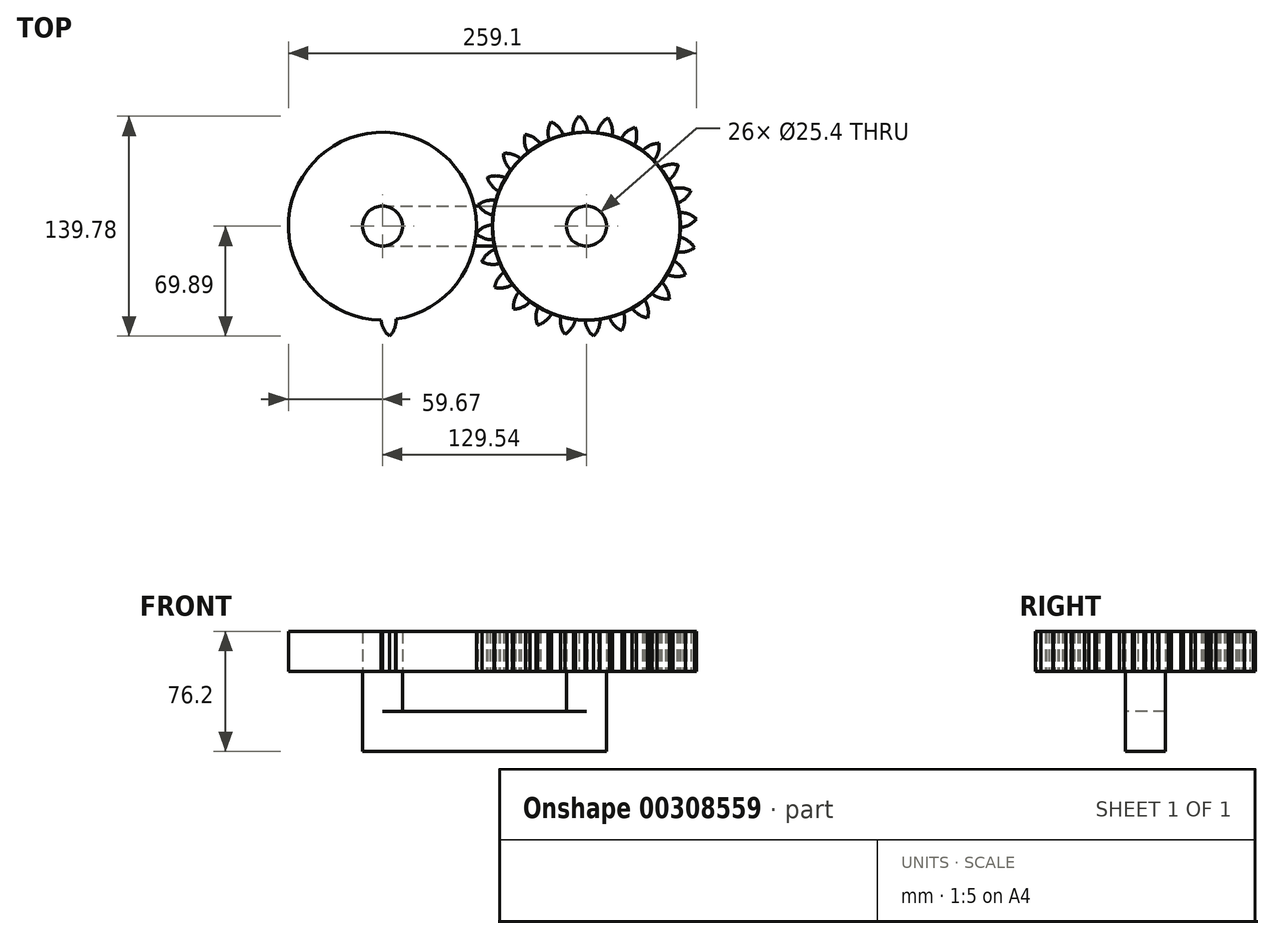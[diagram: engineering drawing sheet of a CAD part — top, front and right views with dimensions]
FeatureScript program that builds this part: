
annotation { "Feature Type Name" : "Feature", "Feature Type Description" : "" }
export const myFeature = defineFeature(function(context is Context, id is Id, definition is map)
    precondition{}
    {
        {
            var Q0;
            Q0=qCreatedBy(makeId("Top.planeOp"),FACE);
            var sketch = newSketch(context, id + "F0", { "sketchPlane" : qUnion([Q0])});
            skLineSegment(sketch, "E0.bottom", {"start": v(-22.49, 9.75) * mm, "end": v(107.05, 9.75) * mm});
            skLineSegment(sketch, "E0.top", {"start": v(-22.49, -15.65) * mm, "end": v(107.05, -15.65) * mm});
            skLineSegment(sketch, "E0.left", {"start": v(-22.49, 9.75) * mm, "end": v(-22.49, -15.65) * mm});
            skLineSegment(sketch, "E0.right", {"start": v(107.05, 9.75) * mm, "end": v(107.05, -15.65) * mm});
            skCircle(sketch, "E1", {"center": v(-22.49, -2.95) * mm, "radius": 12.7 * mm});
            skCircle(sketch, "E2", {"center": v(107.05, -2.95) * mm, "radius": 12.7 * mm});
            skSolve(sketch);
        }
        {
            var Q0;
            {var subQ0=sQuery(id+"F0.wireOp",EDGE,"E0.left");Q0=makeQuery(id+"F0.imprint","IMPRINT",FACE,{"disambiguationData":[TD([[makeQuery(id+"F0.imprint","IMPRINT",EDGE,{"derivedFrom":subQ0}),-1.0]])]});}
            var Q1;
            {var subQ0=sQuery(id+"F0.wireOp",EDGE,"E0.left");Q1=makeQuery(id+"F0.imprint","IMPRINT",FACE,{"disambiguationData":[TD([[makeQuery(id+"F0.imprint","IMPRINT",EDGE,{"derivedFrom":subQ0}),1.0]])]});}
            var Q2;
            {var subQ0=sQuery(id+"F0.wireOp",EDGE,"E0.bottom");Q2=makeQuery(id+"F0.imprint","IMPRINT",FACE,{"disambiguationData":[TD([[makeQuery(id+"F0.imprint","IMPRINT",EDGE,{"derivedFrom":subQ0}),-1.0]])]});}
            var Q3;
            {var subQ0=sQuery(id+"F0.wireOp",EDGE,"E0.right");Q3=makeQuery(id+"F0.imprint","IMPRINT",FACE,{"disambiguationData":[TD([[makeQuery(id+"F0.imprint","IMPRINT",EDGE,{"derivedFrom":subQ0}),-1.0]])]});}
            var Q4;
            {var subQ0=sQuery(id+"F0.wireOp",EDGE,"E0.right");Q4=makeQuery(id+"F0.imprint","IMPRINT",FACE,{"disambiguationData":[TD([[makeQuery(id+"F0.imprint","IMPRINT",EDGE,{"derivedFrom":subQ0}),1.0]])]});}
            extrude(context, id + "F1", {"entities" : qUnion([Q0, Q1, Q2, Q3, Q4]), "depth" : 25.4 * mm});
        }
        {
            var Q0;
            {var subQ0=sQuery(id+"F0.wireOp",EDGE,"E0.right");Q0=makeQuery(id+"F0.imprint","IMPRINT",FACE,{"disambiguationData":[TD([[makeQuery(id+"F0.imprint","IMPRINT",EDGE,{"derivedFrom":subQ0}),1.0]])]});}
            var Q1;
            {var subQ0=sQuery(id+"F0.wireOp",EDGE,"E0.right");Q1=makeQuery(id+"F0.imprint","IMPRINT",FACE,{"disambiguationData":[TD([[makeQuery(id+"F0.imprint","IMPRINT",EDGE,{"derivedFrom":subQ0}),-1.0]])]});}
            var Q2;
            {var subQ0=sQuery(id+"F0.wireOp",EDGE,"E0.left");Q2=makeQuery(id+"F0.imprint","IMPRINT",FACE,{"disambiguationData":[TD([[makeQuery(id+"F0.imprint","IMPRINT",EDGE,{"derivedFrom":subQ0}),1.0]])]});}
            var Q3;
            {var subQ0=sQuery(id+"F0.wireOp",EDGE,"E0.left");Q3=makeQuery(id+"F0.imprint","IMPRINT",FACE,{"disambiguationData":[TD([[makeQuery(id+"F0.imprint","IMPRINT",EDGE,{"derivedFrom":subQ0}),-1.0]])]});}
            extrude(context, id + "F2", {"entities" : qUnion([Q0, Q1, Q2, Q3]), "operationType" : NewBodyOperationType.ADD, "depth" : 50.8 * mm});
        }
        {
            var Q0;
            Q0=makeQuery(id+"F2.opExtrude","CAP_FACE",FACE,{"disambiguationData":[OSD([sQuery(id+"F0.wireOp",EDGE,"E2")])],"isStart":false});
            var sketch = newSketch(context, id + "F3", { "sketchPlane" : qUnion([Q0])});
            skCircle(sketch, "E3", {"center": v(107.05, -2.95) * mm, "radius": 12.7 * mm});
            skCircle(sketch, "E4", {"center": v(107.05, -2.95) * mm, "radius": 53.72 * mm, "construction": true});
            skCircle(sketch, "E5", {"center": v(107.05, -2.95) * mm, "radius": 58.67 * mm, "construction": true});
            skCircle(sketch, "E6", {"center": v(107.05, -2.95) * mm, "radius": 63.5 * mm, "construction": true});
            skLineSegment(sketch, "E7", {"start": v(107.05, -2.95) * mm, "end": v(107.05, -93.43) * mm, "construction": true});
            skLineSegment(sketch, "E8", {"start": v(107.05, -2.95) * mm, "end": v(112.98, -93.47) * mm, "construction": true});
            skCircle(sketch, "E9", {"center": v(107.05, -66.45) * mm, "radius": 14.6 * mm, "construction": true});
            skLineSegment(sketch, "E10", {"start": v(107.05, -66.45) * mm, "end": v(166.51, -66.45) * mm, "construction": true});
            skLineSegment(sketch, "E11", {"start": v(173.53, -42.25) * mm, "end": v(107.05, -66.45) * mm, "construction": true});
            skCircle(sketch, "E12", {"center": v(120.77, -61.45) * mm, "radius": 14.6 * mm, "construction": true});
            skCircle(sketch, "E13", {"center": v(107.05, -2.95) * mm, "radius": 59.67 * mm});
            skArc(sketch, "E14", {"start": v(107.05, -66.45) * mm, "mid": v(108.9, -69.97) * mm, "end": v(111.63, -72.84) * mm});
            skArc(sketch, "E15", {"start": v(106.22, -62.61) * mm, "mid": v(106.5, -64.56) * mm, "end": v(107.05, -66.45) * mm});
            skArc(sketch, "E16.MirrorCS", {"start": v(115.67, -62) * mm, "mid": v(115.64, -63.96) * mm, "end": v(115.34, -65.9) * mm});
            skArc(sketch, "E17.MirrorCS", {"start": v(115.34, -65.9) * mm, "mid": v(113.97, -69.64) * mm, "end": v(111.63, -72.84) * mm});
            skSolve(sketch);
        }
        {
            var Q0;
            Q0=makeQuery(id+"F3.imprint","IMPRINT",FACE,{"disambiguationData":[TD([[makeQuery(id+"F3.imprint","IMPRINT",EDGE,{"derivedFrom":sQuery(id+"F3.wireOp",EDGE,"E14")}),1.0]])]});
            var Q1;
            Q1=makeQuery(id+"F3.imprint","IMPRINT",FACE,{"disambiguationData":[TD([[makeQuery(id+"F3.imprint","IMPRINT",EDGE,{"derivedFrom":sQuery(id+"F3.wireOp",EDGE,"E3")}),-1.0]])]});
            extrude(context, id + "F4", {"entities" : qUnion([Q0, Q1]), "depth" : 25.4 * mm});
        }
        {
            var Q0;
            Q0=makeQuery(id+"F4.opExtrude","SWEPT_BODY",BODY,{"disambiguationData":[OSD([sQuery(id+"F3.wireOp",EDGE,"E3"),sQuery(id+"F3.wireOp",EDGE,"E13"),sQuery(id+"F3.wireOp",EDGE,"E14"),sQuery(id+"F3.wireOp",EDGE,"E15"),sQuery(id+"F3.wireOp",EDGE,"E16.MirrorCS"),sQuery(id+"F3.wireOp",EDGE,"E17.MirrorCS")])]});
            var Q1;
            Q1=makeQuery(id+"F4.opExtrude","SWEPT_FACE",FACE,{"disambiguationData":[OSD([sQuery(id+"F3.wireOp",EDGE,"E13")])]});
            circularPattern(context, id + "F5", {"entities" : qUnion([Q0]), "axis" : qUnion([Q1]), "angle" : 360 * degree, "instanceCount" : 24, "equalSpace" : true});
        }
        {
            var Q0;
            Q0=makeQuery(id+"F4.opExtrude","SWEPT_BODY",BODY,{"disambiguationData":[OSD([sQuery(id+"F3.wireOp",EDGE,"E3"),sQuery(id+"F3.wireOp",EDGE,"E13"),sQuery(id+"F3.wireOp",EDGE,"E14"),sQuery(id+"F3.wireOp",EDGE,"E15"),sQuery(id+"F3.wireOp",EDGE,"E16.MirrorCS"),sQuery(id+"F3.wireOp",EDGE,"E17.MirrorCS")])]});
            transform(context, id + "F6", {"entities" : qUnion([Q0]), "transformType" : TransformType.TRANSLATION_3D, "dx" : -129.54 * mm, "dy" : 0 * mm, "dz" : 0 * mm, "makeCopy" : true});
        }
        {
            var Q0;
            Q0=makeQuery(id+"F4.opExtrude","SWEPT_BODY",BODY,{"disambiguationData":[OSD([sQuery(id+"F3.wireOp",EDGE,"E3"),sQuery(id+"F3.wireOp",EDGE,"E13"),sQuery(id+"F3.wireOp",EDGE,"E14"),sQuery(id+"F3.wireOp",EDGE,"E15"),sQuery(id+"F3.wireOp",EDGE,"E16.MirrorCS"),sQuery(id+"F3.wireOp",EDGE,"E17.MirrorCS")])]});
            transform(context, id + "F7", {"entities" : qUnion([Q0]), "transformType" : TransformType.TRANSLATION_3D, "dx" : 0 * mm, "dy" : 0 * mm, "dz" : 0 * mm, "makeCopy" : true});
        }
    });
